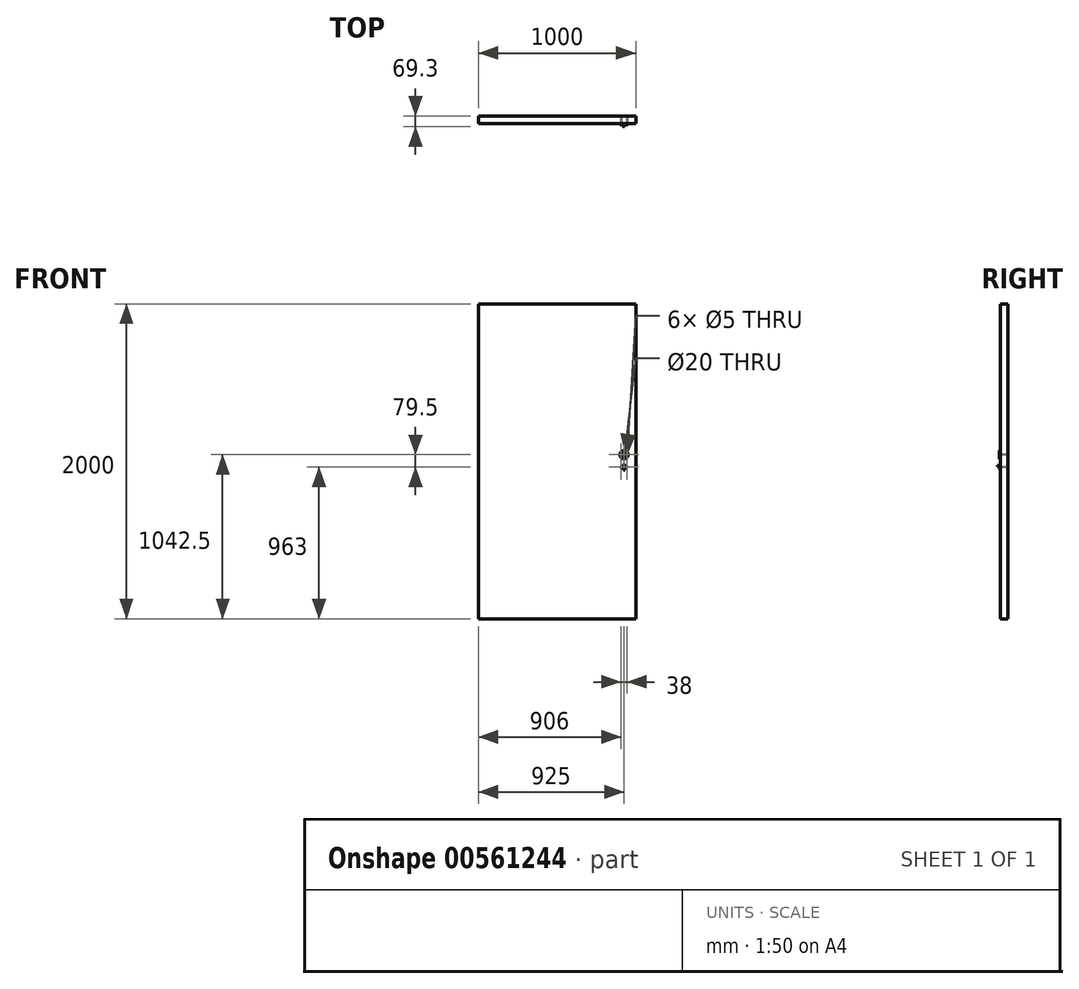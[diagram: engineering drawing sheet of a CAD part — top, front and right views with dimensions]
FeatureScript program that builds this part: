
annotation { "Feature Type Name" : "Feature", "Feature Type Description" : "" }
export const myFeature = defineFeature(function(context is Context, id is Id, definition is map)
    precondition{}
    {
        {
            var Q0;
            Q0=qCreatedBy(makeId("Front.planeOp"),FACE);
            var sketch = newSketch(context, id + "F0", { "sketchPlane" : qUnion([Q0])});
            skLineSegment(sketch, "E0", {"start": v(75, -970) * mm, "end": v(75, 1030) * mm});
            skLineSegment(sketch, "E1", {"start": v(75, 1030) * mm, "end": v(-925, 1030) * mm});
            skLineSegment(sketch, "E2", {"start": v(-925, 1030) * mm, "end": v(-925, -970) * mm});
            skLineSegment(sketch, "E3", {"start": v(-925, -970) * mm, "end": v(75, -970) * mm});
            skSolve(sketch);
        }
        {
            var Q0;
            Q0 = qSketchRegion(id + "F0", true);
            extrude(context, id + "F1", {"entities" : qUnion([Q0]), "oppositeDirection" : true, "depth" : 50 * mm, "offsetDistance" : 25 * mm});
        }
        {
            var Q0;
            Q0=qCreatedBy(makeId("Front.planeOp"),FACE);
            var sketch = newSketch(context, id + "F2", { "sketchPlane" : qUnion([Q0])});
            skCircle(sketch, "E4", {"center": v(0, 0) * mm, "radius": 8.5 * mm});
            skLineSegment(sketch, "E5", {"start": v(25.08, 0) * mm, "end": v(-30.95, 0) * mm, "construction": true});
            skLineSegment(sketch, "E6", {"start": v(0, -84.64) * mm, "end": v(0, 145.15) * mm, "construction": true});
            skLineSegment(sketch, "E7.bottom", {"start": v(5, 0) * mm, "end": v(-5, 0) * mm});
            skLineSegment(sketch, "E7.top", {"start": v(5, -24.5) * mm, "end": v(-5, -24.5) * mm});
            skLineSegment(sketch, "E7.left", {"start": v(5, 0) * mm, "end": v(5, -24.5) * mm});
            skLineSegment(sketch, "E7.right", {"start": v(-5, 0) * mm, "end": v(-5, -24.5) * mm});
            skLineSegment(sketch, "E8", {"start": v(53.96, -7) * mm, "end": v(-45.83, -7) * mm, "construction": true});
            skCircle(sketch, "E9", {"center": v(19, -7) * mm, "radius": 2.5 * mm});
            skCircle(sketch, "E10", {"center": v(-19, -7) * mm, "radius": 2.5 * mm});
            skCircle(sketch, "E11", {"center": v(0, 0) * mm, "radius": 4 * mm});
            skCircle(sketch, "E12", {"center": v(0, 72.5) * mm, "radius": 26 * mm});
            skCircle(sketch, "E13", {"center": v(0, 72.5) * mm, "radius": 10 * mm});
            skLineSegment(sketch, "E14", {"start": v(-55.31, 72.5) * mm, "end": v(67.94, 72.5) * mm, "construction": true});
            skCircle(sketch, "E15", {"center": v(19, 72.5) * mm, "radius": 2.5 * mm});
            skCircle(sketch, "E16", {"center": v(-19, 72.5) * mm, "radius": 2.5 * mm});
            skSolve(sketch);
        }
        {
            var Q0;
            {var subQ0=sQuery(id+"F2.wireOp",EDGE,"E7.left");var subQ1=sQuery(id+"F2.wireOp",EDGE,"E4");var subQ2=makeQuery(id+"F2.imprint","INTERSECT",VERTEX,{"derivedFrom":[subQ1,subQ0]});Q0=makeQuery(id+"F2.imprint","IMPRINT",FACE,{"disambiguationData":[TD([[makeQuery(id+"F2.imprint","IMPRINT",EDGE,{"disambiguationData":[TD([[subQ2,-1.0]])],"derivedFrom":subQ1}),1.0]])]});}
            var Q1;
            {var subQ0=sQuery(id+"F2.wireOp",EDGE,"E7.left");var subQ1=sQuery(id+"F2.wireOp",EDGE,"E4");var subQ2=makeQuery(id+"F2.imprint","INTERSECT",VERTEX,{"derivedFrom":[subQ1,subQ0]});Q1=makeQuery(id+"F2.imprint","IMPRINT",FACE,{"disambiguationData":[TD([[makeQuery(id+"F2.imprint","IMPRINT",EDGE,{"disambiguationData":[TD([[subQ2,1.0]])],"derivedFrom":subQ1}),1.0]])]});}
            var Q2;
            {var subQ5=sQuery(id+"F2.wireOp",EDGE,"E7.top");Q2=makeQuery(id+"F2.imprint","IMPRINT",FACE,{"disambiguationData":[TD([[makeQuery(id+"F2.imprint","IMPRINT",EDGE,{"derivedFrom":subQ5}),-1.0]])]});}
            var Q3;
            {var subQ0=sQuery(id+"F2.wireOp",EDGE,"E11");var subQ1=sQuery(id+"F2.wireOp",EDGE,"E7.bottom");var subQ2=makeQuery(id+"F2.imprint","INTERSECT",VERTEX,{"disambiguationData":[OD(0.0)],"derivedFrom":[subQ1,subQ0]});Q3=makeQuery(id+"F2.imprint","IMPRINT",FACE,{"disambiguationData":[TD([[makeQuery(id+"F2.imprint","IMPRINT",EDGE,{"disambiguationData":[TD([[subQ2,-1.0]])],"derivedFrom":subQ1}),1.0]])]});}
            var Q4;
            {var subQ0=sQuery(id+"F2.wireOp",EDGE,"E11");var subQ1=sQuery(id+"F2.wireOp",EDGE,"E7.bottom");var subQ2=makeQuery(id+"F2.imprint","INTERSECT",VERTEX,{"disambiguationData":[OD(0.0)],"derivedFrom":[subQ1,subQ0]});Q4=makeQuery(id+"F2.imprint","IMPRINT",FACE,{"disambiguationData":[TD([[makeQuery(id+"F2.imprint","IMPRINT",EDGE,{"disambiguationData":[TD([[subQ2,-1.0]])],"derivedFrom":subQ1}),-1.0]])]});}
            extrude(context, id + "F3", {"entities" : qUnion([Q0, Q1, Q2, Q3, Q4]), "depth" : 3.5 * mm, "offsetDistance" : 25 * mm});
        }
        {
            var Q0;
            Q0=makeQuery(id+"F2.imprint","IMPRINT",FACE,{"disambiguationData":[TD([[makeQuery(id+"F2.imprint","IMPRINT",EDGE,{"derivedFrom":sQuery(id+"F2.wireOp",EDGE,"E12")}),1.0]])]});
            extrude(context, id + "F4", {"entities" : qUnion([Q0]), "depth" : 5 * mm, "offsetDistance" : 25 * mm});
        }
        {
            var Q0;
            Q0=makeQuery(id+"F2.imprint","IMPRINT",FACE,{"disambiguationData":[TD([[makeQuery(id+"F2.imprint","IMPRINT",EDGE,{"derivedFrom":sQuery(id+"F2.wireOp",EDGE,"E10")}),1.0]])]});
            var Q1;
            Q1=makeQuery(id+"F2.imprint","IMPRINT",FACE,{"disambiguationData":[TD([[makeQuery(id+"F2.imprint","IMPRINT",EDGE,{"derivedFrom":sQuery(id+"F2.wireOp",EDGE,"E9")}),1.0]])]});
            var Q2;
            Q2=makeQuery(id+"F2.imprint","IMPRINT",FACE,{"disambiguationData":[TD([[makeQuery(id+"F2.imprint","IMPRINT",EDGE,{"derivedFrom":sQuery(id+"F2.wireOp",EDGE,"E15")}),1.0]])]});
            var Q3;
            Q3=makeQuery(id+"F2.imprint","IMPRINT",FACE,{"disambiguationData":[TD([[makeQuery(id+"F2.imprint","IMPRINT",EDGE,{"derivedFrom":sQuery(id+"F2.wireOp",EDGE,"E16")}),1.0]])]});
            var Q4;
            Q4=makeQuery(id+"F1.opExtrude","CAP_FACE",FACE,{"disambiguationData":[OSD([sQuery(id+"F0.wireOp",EDGE,"E0"),sQuery(id+"F0.wireOp",EDGE,"E1"),sQuery(id+"F0.wireOp",EDGE,"E2"),sQuery(id+"F0.wireOp",EDGE,"E3")])],"isStart":false});
            extrude(context, id + "F5", {"entities" : qUnion([Q0, Q1, Q2, Q3]), "operationType" : NewBodyOperationType.REMOVE, "endBound" : BoundingType.UP_TO_SURFACE, "oppositeDirection" : true, "depth" : 25 * mm, "endBoundEntityFace" : qUnion([Q4]), "offsetDistance" : 25 * mm});
        }
        {
            var Q0;
            Q0=makeQuery(id+"F3.opExtrude","CAP_FACE",FACE,{"disambiguationData":[OSD([sQuery(id+"F2.wireOp",EDGE,"E4"),sQuery(id+"F2.wireOp",EDGE,"E7.top"),sQuery(id+"F2.wireOp",EDGE,"E7.left"),sQuery(id+"F2.wireOp",EDGE,"E7.right")])],"isStart":false});
            var sketch = newSketch(context, id + "F6", { "sketchPlane" : qUnion([Q0])});
            skCircle(sketch, "E17", {"center": v(0, 0) * mm, "radius": 4 * mm});
            skLineSegment(sketch, "E18", {"start": v(2.7, 2.95) * mm, "end": v(-2.7, 2.95) * mm});
            skSolve(sketch);
        }
        {
            var Q0;
            {var subQ0=sQuery(id+"F6.wireOp",EDGE,"E18");Q0=makeQuery(id+"F6.imprint","IMPRINT",FACE,{"disambiguationData":[TD([[makeQuery(id+"F6.imprint","IMPRINT",EDGE,{"derivedFrom":subQ0}),1.0]])]});}
            extrude(context, id + "F7", {"entities" : qUnion([Q0]), "operationType" : NewBodyOperationType.ADD, "depth" : 15.8 * mm, "offsetDistance" : 25 * mm});
        }
    });
